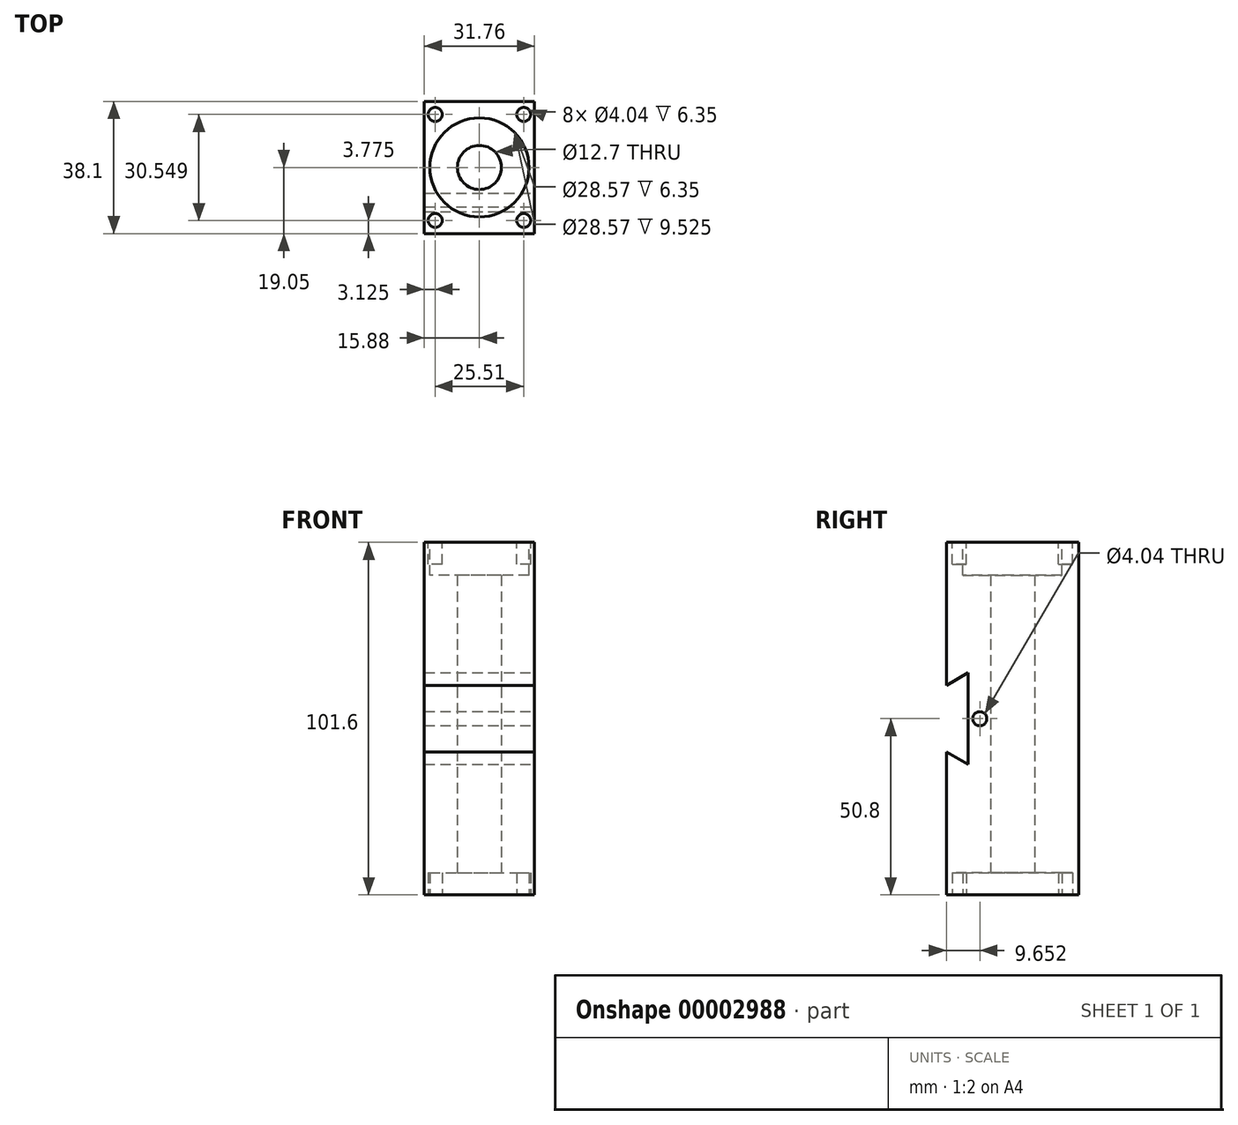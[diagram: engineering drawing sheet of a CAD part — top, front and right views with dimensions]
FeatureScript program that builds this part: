
annotation { "Feature Type Name" : "Feature", "Feature Type Description" : "" }
export const myFeature = defineFeature(function(context is Context, id is Id, definition is map)
    precondition{}
    {
        {
            var Q0;
            Q0=qCreatedBy(makeId("Top.planeOp"),FACE);
            var sketch = newSketch(context, id + "F0", { "sketchPlane" : qUnion([Q0])});
            skLineSegment(sketch, "E0.rect.bottom", {"start": v(15.87, -19.05) * mm, "end": v(-15.88, -19.05) * mm});
            skLineSegment(sketch, "E0.rect.top", {"start": v(15.87, 19.05) * mm, "end": v(-15.87, 19.05) * mm});
            skLineSegment(sketch, "E0.rect.left", {"start": v(15.87, -19.05) * mm, "end": v(15.87, 19.05) * mm});
            skLineSegment(sketch, "E0.rect.right", {"start": v(-15.88, -19.05) * mm, "end": v(-15.88, 19.05) * mm});
            skPoint(sketch, "E0.rect.middle", {"position": v(0, 0) * mm});
            skCircle(sketch, "E1", {"center": v(0, 0) * mm, "radius": 6.35 * mm});
            skSolve(sketch);
        }
        {
            var Q0;
            Q0 = qSketchRegion(id + "F0", true);
            extrude(context, id + "F1", {"entities" : qUnion([Q0]), "endBound" : BoundingType.SYMMETRIC, "depth" : 101.6 * mm});
        }
        {
            var Q0;
            Q0=makeQuery(id+"F1.opExtrude","SWEPT_FACE",FACE,{"disambiguationData":[OSD([sQuery(id+"F0.wireOp",EDGE,"E0.rect.left")])]});
            var sketch = newSketch(context, id + "F2", { "sketchPlane" : qUnion([Q0])});
            skLineSegment(sketch, "E2.rect.left", {"start": v(-12.72, -13.2) * mm, "end": v(-12.72, 13.2) * mm});
            skPoint(sketch, "E2.rect.middle", {"position": v(-19.05, 0) * mm});
            skLineSegment(sketch, "E3", {"start": v(-12.72, 13.2) * mm, "end": v(-19.05, 9.56) * mm});
            skLineSegment(sketch, "E4", {"start": v(-12.72, -13.2) * mm, "end": v(-19.05, -9.56) * mm});
            skPoint(sketch, "E2.rect.right.start.orphan", {"position": v(-25.38, -13.2) * mm});
            skPoint(sketch, "E2.rect.top.end.orphan", {"position": v(-25.38, 13.2) * mm});
            skLineSegment(sketch, "E5", {"start": v(-19.05, -9.56) * mm, "end": v(-19.05, 9.56) * mm});
            skSolve(sketch);
        }
        {
            var Q0;
            Q0=makeQuery(id+"F2.imprint","IMPRINT",FACE,{"disambiguationData":[TD([[makeQuery(id+"F2.imprint","IMPRINT",EDGE,{"derivedFrom":sQuery(id+"F2.wireOp",EDGE,"E2.rect.left")}),1.0]])]});
            extrude(context, id + "F3", {"entities" : qUnion([Q0]), "operationType" : NewBodyOperationType.REMOVE, "endBound" : BoundingType.THROUGH_ALL, "oppositeDirection" : true, "depth" : 25.4 * mm});
        }
        {
            var Q0;
            Q0=makeQuery(id+"F1.opExtrude","CAP_FACE",FACE,{"disambiguationData":[OSD([sQuery(id+"F0.wireOp",EDGE,"E0.rect.bottom"),sQuery(id+"F0.wireOp",EDGE,"E0.rect.top"),sQuery(id+"F0.wireOp",EDGE,"E0.rect.left"),sQuery(id+"F0.wireOp",EDGE,"E0.rect.right"),sQuery(id+"F0.wireOp",EDGE,"E1")])],"isStart":true});
            var sketch = newSketch(context, id + "F4", { "sketchPlane" : qUnion([Q0])});
            skCircle(sketch, "E6", {"center": v(0, 0) * mm, "radius": 14.29 * mm});
            skSolve(sketch);
        }
        {
            var Q0;
            Q0 = qSketchRegion(id + "F4", true);
            extrude(context, id + "F5", {"entities" : qUnion([Q0]), "operationType" : NewBodyOperationType.REMOVE, "oppositeDirection" : true, "depth" : 6.35 * mm});
        }
        {
            var Q0;
            Q0=makeQuery(id+"F1.opExtrude","CAP_FACE",FACE,{"disambiguationData":[OSD([sQuery(id+"F0.wireOp",EDGE,"E0.rect.bottom"),sQuery(id+"F0.wireOp",EDGE,"E0.rect.top"),sQuery(id+"F0.wireOp",EDGE,"E0.rect.left"),sQuery(id+"F0.wireOp",EDGE,"E0.rect.right"),sQuery(id+"F0.wireOp",EDGE,"E1")])],"isStart":false});
            var sketch = newSketch(context, id + "F6", { "sketchPlane" : qUnion([Q0])});
            skCircle(sketch, "E7", {"center": v(0, 0) * mm, "radius": 14.29 * mm});
            skSolve(sketch);
        }
        {
            var Q0;
            Q0 = qSketchRegion(id + "F6", true);
            extrude(context, id + "F7", {"entities" : qUnion([Q0]), "operationType" : NewBodyOperationType.REMOVE, "oppositeDirection" : true, "depth" : 9.52 * mm});
        }
        {
            var Q0;
            Q0=makeQuery(id+"F1.opExtrude","SWEPT_FACE",FACE,{"disambiguationData":[OSD([sQuery(id+"F0.wireOp",EDGE,"E0.rect.left")])]});
            var sketch = newSketch(context, id + "F8", { "sketchPlane" : qUnion([Q0])});
            skCircle(sketch, "E8", {"center": v(-9.4, 0) * mm, "radius": 2.02 * mm});
            skSolve(sketch);
        }
        {
            var Q0;
            Q0=makeQuery(id+"F8.imprint","IMPRINT",FACE,{"disambiguationData":[TD([[makeQuery(id+"F8.imprint","IMPRINT",EDGE,{"derivedFrom":sQuery(id+"F8.wireOp",EDGE,"E8")}),1.0]])]});
            extrude(context, id + "F9", {"entities" : qUnion([Q0]), "operationType" : NewBodyOperationType.REMOVE, "endBound" : BoundingType.THROUGH_ALL, "oppositeDirection" : true, "depth" : 25.4 * mm});
        }
        {
            var Q0;
            Q0=makeQuery(id+"F1.opExtrude","CAP_FACE",FACE,{"disambiguationData":[OSD([sQuery(id+"F0.wireOp",EDGE,"E0.rect.bottom"),sQuery(id+"F0.wireOp",EDGE,"E0.rect.top"),sQuery(id+"F0.wireOp",EDGE,"E0.rect.left"),sQuery(id+"F0.wireOp",EDGE,"E0.rect.right"),sQuery(id+"F0.wireOp",EDGE,"E1")])],"isStart":false});
            var sketch = newSketch(context, id + "F10", { "sketchPlane" : qUnion([Q0])});
            skCircle(sketch, "E9", {"center": v(-12.75, 15.27) * mm, "radius": 2.02 * mm});
            skLineSegment(sketch, "E10", {"start": v(0, 0) * mm, "end": v(0, 20.3) * mm, "construction": true});
            skLineSegment(sketch, "E11", {"start": v(0, 0) * mm, "end": v(-17.92, 21.36) * mm, "construction": true});
            skCircle(sketch, "E12.0.MirrorC", {"center": v(12.75, 15.27) * mm, "radius": 2.02 * mm});
            skLineSegment(sketch, "E13", {"start": v(0, 0) * mm, "end": v(-17.13, 0) * mm, "construction": true});
            skCircle(sketch, "E14.0.MirrorC", {"center": v(-12.75, -15.27) * mm, "radius": 2.02 * mm});
            skCircle(sketch, "E15.0.MirrorC", {"center": v(12.75, -15.27) * mm, "radius": 2.02 * mm});
            skSolve(sketch);
        }
        {
            var Q0;
            Q0 = qSketchRegion(id + "F10", true);
            extrude(context, id + "F11", {"entities" : qUnion([Q0]), "operationType" : NewBodyOperationType.REMOVE, "oppositeDirection" : true, "depth" : 6.35 * mm});
        }
        {
            var Q0;
            Q0=makeQuery(id+"F1.opExtrude","CAP_FACE",FACE,{"disambiguationData":[OSD([sQuery(id+"F0.wireOp",EDGE,"E0.rect.bottom"),sQuery(id+"F0.wireOp",EDGE,"E0.rect.top"),sQuery(id+"F0.wireOp",EDGE,"E0.rect.left"),sQuery(id+"F0.wireOp",EDGE,"E0.rect.right"),sQuery(id+"F0.wireOp",EDGE,"E1")])],"isStart":true});
            var sketch = newSketch(context, id + "F12", { "sketchPlane" : qUnion([Q0])});
            skCircle(sketch, "E16.0", {"center": v(12.75, -15.27) * mm, "radius": 2.02 * mm});
            skCircle(sketch, "E17.0", {"center": v(-12.75, -15.27) * mm, "radius": 2.02 * mm});
            skCircle(sketch, "E18.0", {"center": v(-12.75, 15.27) * mm, "radius": 2.02 * mm});
            skCircle(sketch, "E19.0", {"center": v(12.75, 15.27) * mm, "radius": 2.02 * mm});
            skSolve(sketch);
        }
        {
            var Q0;
            Q0=makeQuery(id+"F12.imprint","IMPRINT",FACE,{"disambiguationData":[TD([[makeQuery(id+"F12.imprint","IMPRINT",EDGE,{"derivedFrom":sQuery(id+"F12.wireOp",EDGE,"E17.0")}),1.0]])]});
            var Q1;
            Q1=makeQuery(id+"F12.imprint","IMPRINT",FACE,{"disambiguationData":[TD([[makeQuery(id+"F12.imprint","IMPRINT",EDGE,{"derivedFrom":sQuery(id+"F12.wireOp",EDGE,"E18.0")}),1.0]])]});
            var Q2;
            Q2=makeQuery(id+"F12.imprint","IMPRINT",FACE,{"disambiguationData":[TD([[makeQuery(id+"F12.imprint","IMPRINT",EDGE,{"derivedFrom":sQuery(id+"F12.wireOp",EDGE,"E19.0")}),1.0]])]});
            var Q3;
            Q3=makeQuery(id+"F12.imprint","IMPRINT",FACE,{"disambiguationData":[TD([[makeQuery(id+"F12.imprint","IMPRINT",EDGE,{"derivedFrom":sQuery(id+"F12.wireOp",EDGE,"E16.0")}),1.0]])]});
            extrude(context, id + "F13", {"entities" : qUnion([Q0, Q1, Q2, Q3]), "operationType" : NewBodyOperationType.REMOVE, "oppositeDirection" : true, "depth" : 6.35 * mm});
        }
    });
